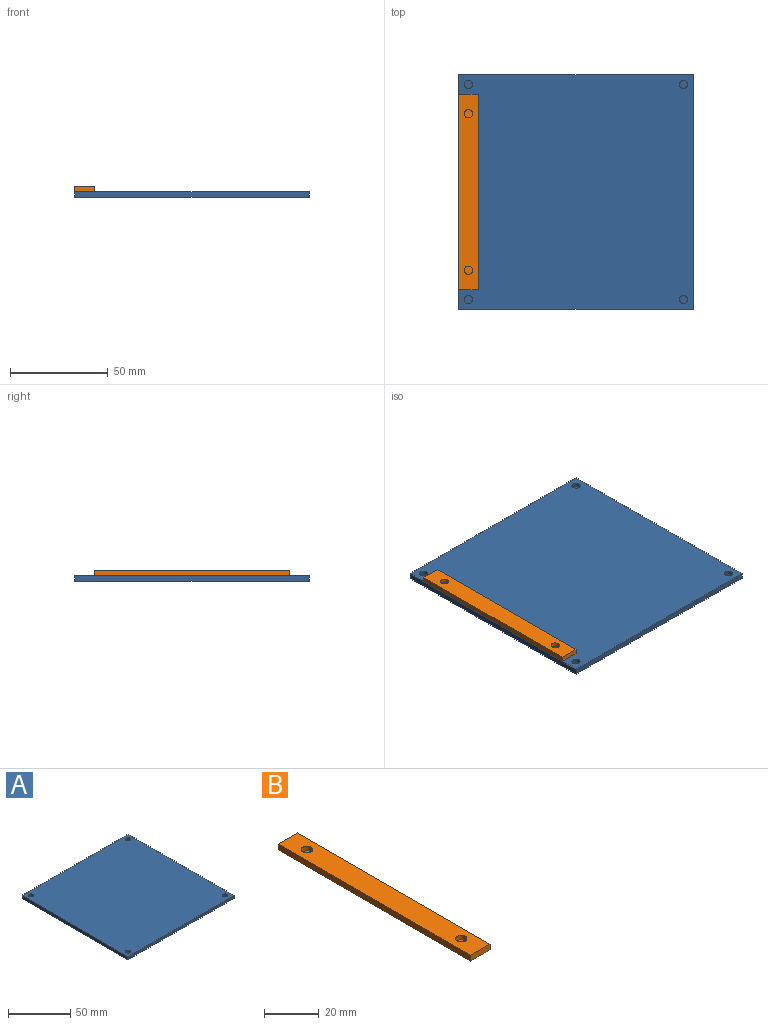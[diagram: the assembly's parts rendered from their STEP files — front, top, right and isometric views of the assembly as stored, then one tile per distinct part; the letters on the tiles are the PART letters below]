
ASSEMBLY  parts=2 mates=1
PART A: 14 faces, bbox 120x120x3 mm
  f0: plane 120x3mm, normal (0,1,0), area 360mm2, adj f1,f3,f4,f5
  f1: plane 120x3mm, normal (-1,0,0), area 360mm2, adj f0,f2,f4,f5
  f2: plane 120x3mm, normal (0,-1,0), area 360mm2, adj f1,f3,f4,f5
  f3: plane 120x3mm, normal (1,0,0), area 360mm2, adj f0,f2,f4,f5
  f4: plane 120x120mm, normal (0,0,1), area 14344.6mm2, adj f0,f1,f2,f3,f6,f8,f10,f12
  f5: plane 120x120mm, normal (0,0,-1), area 14400mm2, adj f0,f1,f2,f3
  f6: cylinder r=2.1mm len=4.2mm, axis (0,0,1), area 26.4mm2, adj f4,f7
  f7: plane 4.2x4.2mm, normal (0,0,1), area 13.9mm2, adj f6
  f8: cylinder r=2.1mm len=4.2mm, axis (0,0,1), area 26.4mm2, adj f4,f9
  f9: plane 4.2x4.2mm, normal (0,0,1), area 13.9mm2, adj f8
  f10: cylinder r=2.1mm len=4.2mm, axis (0,0,1), area 26.4mm2, adj f4,f11
  f11: plane 4.2x4.2mm, normal (0,0,1), area 13.9mm2, adj f10
  f12: cylinder r=2.1mm len=4.2mm, axis (0,0,1), area 26.4mm2, adj f4,f13
  f13: plane 4.2x4.2mm, normal (0,0,1), area 13.9mm2, adj f12
PART B: 10 faces, bbox 10x100x2.6 mm
  f0: plane 10x2.6mm, normal (0,1,0), area 26mm2, adj f1,f3,f4,f5
  f1: plane 100x2.6mm, normal (-1,0,0), area 260mm2, adj f0,f2,f4,f5
  f2: plane 10x2.6mm, normal (0,-1,0), area 26mm2, adj f1,f3,f4,f5
  f3: plane 100x2.6mm, normal (1,0,0), area 260mm2, adj f0,f2,f4,f5
  f4: plane 100x10mm, normal (0,0,1), area 972.3mm2, adj f0,f1,f2,f3,f6,f8
  f5: plane 100x10mm, normal (0,0,-1), area 1000mm2, adj f0,f1,f2,f3
  f6: cylinder r=2.1mm len=4.2mm, axis (0,0,1), area 26.4mm2, adj f4,f7
  f7: plane 4.2x4.2mm, normal (0,0,1), area 13.9mm2, adj f6
  f8: cylinder r=2.1mm len=4.2mm, axis (0,0,1), area 26.4mm2, adj f4,f9
  f9: plane 4.2x4.2mm, normal (0,0,1), area 13.9mm2, adj f8
PLACE A t=(60,60,1.5)mm
PLACE B t=(5,60,3)mm
MATE fastened B.f5 <-> A.f4  axis (0,0,-1) through (0,60,3)mm
